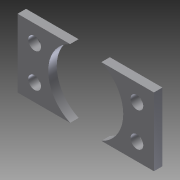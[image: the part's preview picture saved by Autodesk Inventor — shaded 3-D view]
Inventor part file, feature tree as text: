
AUTODESK INVENTOR PART (.ipt)
format: ipt  version: 2011 (Build 150239000, 239)  size: 94,208 bytes
history: native  units: in
note: dims shown in document units (in); Inventor stores cm internally (conversion verified against a paired STEP export)
features: sketch x3, extrude x2, hole x1
ambient origin geometry x8: Origin, YZ Plane, XZ Plane, XY Plane, X Axis, Y Axis, Z Axis, Center Point
bodies: Solid1 (feature_tree)
feature tree (6):
  extrude  "Extrusion1"  Depth=0.5in
  extrude  "Extrusion2"  Depth=0.55in
  hole  "Hole3"  [1 undecoded]
  sketch  "Sketch1"  dims[d0=1.0in d1=0.5in]
  sketch  "Sketch2"  dims[d2=0.0625in d3=0.0in d4=0.55in]
  sketch  "Sketch6"  dims[d5=0.0625in d6=0.0in d21=0.094in d22=0.75in d23=0.375in d24=0.25in d25=0.5635in d26=1.0in d27=0.8108in]
note: 1 required parameter value undecoded (feature->parameter linkage not recoverable at this tier; creation-order binding heuristic only, values carry confidence <= 0.55)
